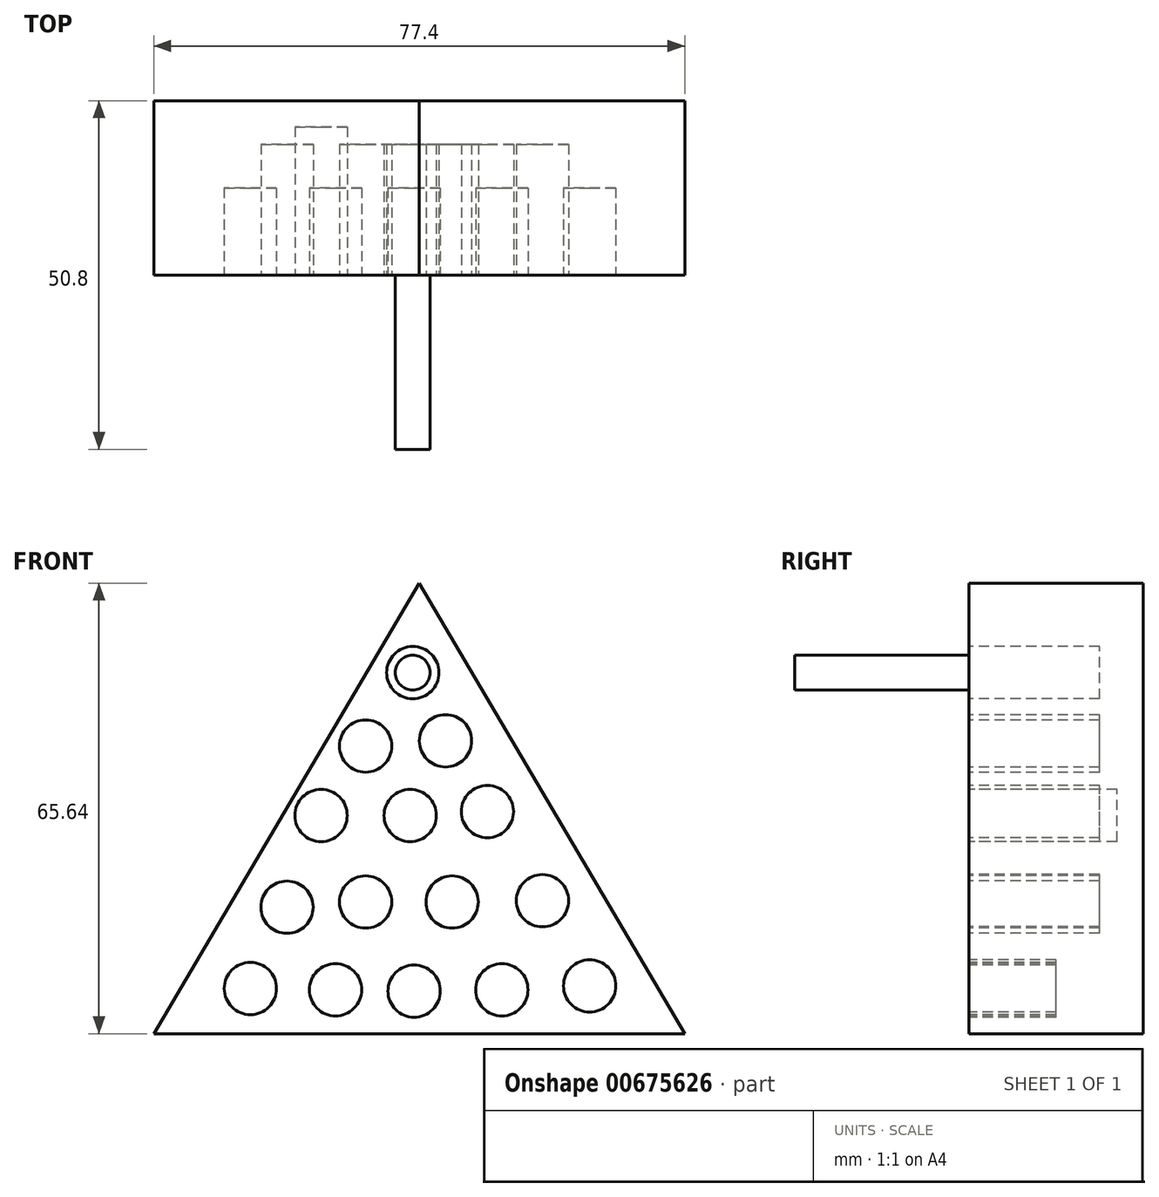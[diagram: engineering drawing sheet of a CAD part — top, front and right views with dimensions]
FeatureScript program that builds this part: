
annotation { "Feature Type Name" : "Feature", "Feature Type Description" : "" }
export const myFeature = defineFeature(function(context is Context, id is Id, definition is map)
    precondition{}
    {
        {
            var Q0;
            Q0=qCreatedBy(makeId("Front.planeOp"),FACE);
            var sketch = newSketch(context, id + "F0", { "sketchPlane" : qUnion([Q0])});
            skLineSegment(sketch, "E0", {"start": v(0, 0) * mm, "end": v(-38.7, 65.64) * mm});
            skLineSegment(sketch, "E1", {"start": v(-38.7, 65.64) * mm, "end": v(-77.4, 0) * mm});
            skLineSegment(sketch, "E2", {"start": v(-77.4, 0) * mm, "end": v(0, 0) * mm});
            skSolve(sketch);
        }
        {
            var Q0;
            Q0=makeQuery(id+"F0.imprint","IMPRINT",FACE,{"disambiguationData":[TD([[makeQuery(id+"F0.imprint","IMPRINT",EDGE,{"derivedFrom":sQuery(id+"F0.wireOp",EDGE,"E0")}),1.0]])]});
            extrude(context, id + "F1", {"entities" : qUnion([Q0]), "depth" : 25.4 * mm, "offsetDistance" : 25.4 * mm});
        }
        {
            var Q0;
            Q0=makeQuery(id+"F1.opExtrude","CAP_FACE",FACE,{"disambiguationData":[OSD([sQuery(id+"F0.wireOp",EDGE,"E0"),sQuery(id+"F0.wireOp",EDGE,"E1"),sQuery(id+"F0.wireOp",EDGE,"E2")])],"isStart":false});
            var sketch = newSketch(context, id + "F2", { "sketchPlane" : qUnion([Q0])});
            skCircle(sketch, "E3", {"center": v(-63.33, 6.59) * mm, "radius": 3.81 * mm});
            skCircle(sketch, "E4", {"center": v(-50.92, 6.4) * mm, "radius": 3.81 * mm});
            skCircle(sketch, "E5", {"center": v(-39.46, 6.2) * mm, "radius": 3.81 * mm});
            skCircle(sketch, "E6", {"center": v(-26.67, 6.4) * mm, "radius": 3.81 * mm});
            skCircle(sketch, "E7", {"center": v(-13.87, 6.97) * mm, "radius": 3.81 * mm});
            skSolve(sketch);
        }
        {
            var Q0;
            Q0 = qSketchRegion(id + "F2", true);
            extrude(context, id + "F3", {"entities" : qUnion([Q0]), "operationType" : NewBodyOperationType.REMOVE, "oppositeDirection" : true, "depth" : 12.7 * mm, "offsetDistance" : 25.4 * mm});
        }
        {
            var Q0;
            Q0=makeQuery(id+"F1.opExtrude","CAP_FACE",FACE,{"disambiguationData":[OSD([sQuery(id+"F0.wireOp",EDGE,"E0"),sQuery(id+"F0.wireOp",EDGE,"E1"),sQuery(id+"F0.wireOp",EDGE,"E2")])],"isStart":false});
            var sketch = newSketch(context, id + "F4", { "sketchPlane" : qUnion([Q0])});
            skCircle(sketch, "E8", {"center": v(-57.6, 19) * mm, "radius": 3.81 * mm});
            skSolve(sketch);
        }
        {
            var Q0;
            Q0=makeQuery(id+"F4.imprint","IMPRINT",FACE,{"disambiguationData":[TD([[makeQuery(id+"F4.imprint","IMPRINT",EDGE,{"derivedFrom":sQuery(id+"F4.wireOp",EDGE,"E8")}),-1.0]])]});
            var sketch = newSketch(context, id + "F5", { "sketchPlane" : qUnion([Q0])});
            skCircle(sketch, "E9", {"center": v(-46.52, 19.2) * mm, "radius": 3.81 * mm});
            skSolve(sketch);
        }
        {
            var Q0;
            Q0=makeQuery(id+"F4.imprint","IMPRINT",FACE,{"disambiguationData":[TD([[makeQuery(id+"F4.imprint","IMPRINT",EDGE,{"derivedFrom":sQuery(id+"F4.wireOp",EDGE,"E8")}),-1.0]])]});
            var sketch = newSketch(context, id + "F6", { "sketchPlane" : qUnion([Q0])});
            skCircle(sketch, "E10", {"center": v(-33.92, 19.2) * mm, "radius": 3.81 * mm});
            skSolve(sketch);
        }
        {
            var Q0;
            Q0=makeQuery(id+"F4.imprint","IMPRINT",FACE,{"disambiguationData":[TD([[makeQuery(id+"F4.imprint","IMPRINT",EDGE,{"derivedFrom":sQuery(id+"F4.wireOp",EDGE,"E8")}),-1.0]])]});
            var sketch = newSketch(context, id + "F7", { "sketchPlane" : qUnion([Q0])});
            skCircle(sketch, "E11", {"center": v(-20.75, 19.38) * mm, "radius": 3.81 * mm});
            skSolve(sketch);
        }
        {
            var Q0;
            Q0=makeQuery(id+"F4.imprint","IMPRINT",FACE,{"disambiguationData":[TD([[makeQuery(id+"F4.imprint","IMPRINT",EDGE,{"derivedFrom":sQuery(id+"F4.wireOp",EDGE,"E8")}),-1.0]])]});
            var sketch = newSketch(context, id + "F8", { "sketchPlane" : qUnion([Q0])});
            skCircle(sketch, "E12", {"center": v(-40.03, 31.8) * mm, "radius": 3.81 * mm});
            skSolve(sketch);
        }
        {
            var Q0;
            Q0=makeQuery(id+"F4.imprint","IMPRINT",FACE,{"disambiguationData":[TD([[makeQuery(id+"F4.imprint","IMPRINT",EDGE,{"derivedFrom":sQuery(id+"F4.wireOp",EDGE,"E8")}),-1.0]])]});
            var sketch = newSketch(context, id + "F9", { "sketchPlane" : qUnion([Q0])});
            skCircle(sketch, "E13", {"center": v(-53.02, 31.8) * mm, "radius": 3.81 * mm});
            skSolve(sketch);
        }
        {
            var Q0;
            Q0=makeQuery(id+"F7.imprint","IMPRINT",FACE,{"disambiguationData":[TD([[makeQuery(id+"F7.imprint","IMPRINT",EDGE,{"derivedFrom":sQuery(id+"F7.wireOp",EDGE,"E11")}),-1.0]])]});
            var sketch = newSketch(context, id + "F10", { "sketchPlane" : qUnion([Q0])});
            skCircle(sketch, "E14", {"center": v(-28.77, 32.37) * mm, "radius": 3.81 * mm});
            skSolve(sketch);
        }
        {
            var Q0;
            Q0=makeQuery(id+"F4.imprint","IMPRINT",FACE,{"disambiguationData":[TD([[makeQuery(id+"F4.imprint","IMPRINT",EDGE,{"derivedFrom":sQuery(id+"F4.wireOp",EDGE,"E8")}),-1.0]])]});
            var sketch = newSketch(context, id + "F11", { "sketchPlane" : qUnion([Q0])});
            skCircle(sketch, "E15", {"center": v(-46.52, 41.91) * mm, "radius": 3.81 * mm});
            skSolve(sketch);
        }
        {
            var Q0;
            Q0=makeQuery(id+"F4.imprint","IMPRINT",FACE,{"disambiguationData":[TD([[makeQuery(id+"F4.imprint","IMPRINT",EDGE,{"derivedFrom":sQuery(id+"F4.wireOp",EDGE,"E8")}),-1.0]])]});
            var sketch = newSketch(context, id + "F12", { "sketchPlane" : qUnion([Q0])});
            skCircle(sketch, "E16", {"center": v(-34.88, 42.68) * mm, "radius": 3.81 * mm});
            skSolve(sketch);
        }
        {
            var Q0;
            Q0=makeQuery(id+"F4.imprint","IMPRINT",FACE,{"disambiguationData":[TD([[makeQuery(id+"F4.imprint","IMPRINT",EDGE,{"derivedFrom":sQuery(id+"F4.wireOp",EDGE,"E8")}),-1.0]])]});
            var sketch = newSketch(context, id + "F13", { "sketchPlane" : qUnion([Q0])});
            skCircle(sketch, "E17", {"center": v(-39.65, 52.6) * mm, "radius": 3.81 * mm});
            skSolve(sketch);
        }
        {
            var Q0;
            Q0=makeQuery(id+"F4.imprint","IMPRINT",FACE,{"disambiguationData":[TD([[makeQuery(id+"F4.imprint","IMPRINT",EDGE,{"derivedFrom":sQuery(id+"F4.wireOp",EDGE,"E8")}),1.0]])]});
            extrude(context, id + "F14", {"entities" : qUnion([Q0]), "operationType" : NewBodyOperationType.REMOVE, "depth" : 25.4 * mm, "offsetDistance" : 25.4 * mm});
        }
        {
            var Q0;
            Q0=makeQuery(id+"F5.imprint","IMPRINT",FACE,{"disambiguationData":[TD([[makeQuery(id+"F5.imprint","IMPRINT",EDGE,{"derivedFrom":makeQuery(id+"F4.imprint","IMPRINT",EDGE,{"derivedFrom":sQuery(id+"F4.wireOp",EDGE,"E8")})}),1.0]])]});
            var sketch = newSketch(context, id + "F15", { "sketchPlane" : qUnion([Q0])});
            skCircle(sketch, "E18", {"center": v(-57.98, 18.43) * mm, "radius": 3.81 * mm});
            skSolve(sketch);
        }
        {
            var Q0;
            Q0 = qSketchRegion(id + "F5", true);
            extrude(context, id + "F16", {"entities" : qUnion([Q0]), "operationType" : NewBodyOperationType.REMOVE, "oppositeDirection" : true, "depth" : 19.05 * mm, "offsetDistance" : 25.4 * mm});
        }
        {
            var Q0;
            Q0 = qSketchRegion(id + "F6", true);
            extrude(context, id + "F17", {"entities" : qUnion([Q0]), "operationType" : NewBodyOperationType.REMOVE, "oppositeDirection" : true, "depth" : 19.05 * mm, "offsetDistance" : 25.4 * mm});
        }
        {
            var Q0;
            Q0 = qSketchRegion(id + "F8", true);
            extrude(context, id + "F18", {"entities" : qUnion([Q0]), "operationType" : NewBodyOperationType.REMOVE, "oppositeDirection" : true, "depth" : 19.05 * mm, "offsetDistance" : 25.4 * mm});
        }
        {
            var Q0;
            Q0 = qSketchRegion(id + "F7", true);
            extrude(context, id + "F19", {"entities" : qUnion([Q0]), "operationType" : NewBodyOperationType.REMOVE, "oppositeDirection" : true, "depth" : 19.05 * mm, "offsetDistance" : 25.4 * mm});
        }
        {
            var Q0;
            Q0 = qSketchRegion(id + "F12", true);
            extrude(context, id + "F20", {"entities" : qUnion([Q0]), "operationType" : NewBodyOperationType.REMOVE, "oppositeDirection" : true, "depth" : 19.05 * mm, "offsetDistance" : 25.4 * mm});
        }
        {
            var Q0;
            Q0 = qSketchRegion(id + "F13", true);
            extrude(context, id + "F21", {"entities" : qUnion([Q0]), "operationType" : NewBodyOperationType.REMOVE, "oppositeDirection" : true, "depth" : 19.05 * mm, "offsetDistance" : 25.4 * mm});
        }
        {
            var Q0;
            Q0 = qSketchRegion(id + "F11", true);
            extrude(context, id + "F22", {"entities" : qUnion([Q0]), "operationType" : NewBodyOperationType.REMOVE, "oppositeDirection" : true, "depth" : 19.05 * mm, "offsetDistance" : 25.4 * mm});
        }
        {
            var Q0;
            Q0 = qSketchRegion(id + "F9", true);
            extrude(context, id + "F23", {"entities" : qUnion([Q0]), "operationType" : NewBodyOperationType.REMOVE, "oppositeDirection" : true, "depth" : 21.59 * mm, "offsetDistance" : 25.4 * mm});
        }
        {
            var Q0;
            Q0 = qSketchRegion(id + "F15", true);
            extrude(context, id + "F24", {"entities" : qUnion([Q0]), "operationType" : NewBodyOperationType.REMOVE, "oppositeDirection" : true, "depth" : 19.05 * mm, "offsetDistance" : 25.4 * mm});
        }
        {
            var Q0;
            Q0 = qSketchRegion(id + "F10", true);
            extrude(context, id + "F25", {"entities" : qUnion([Q0]), "operationType" : NewBodyOperationType.REMOVE, "oppositeDirection" : true, "depth" : 19.05 * mm, "offsetDistance" : 25.4 * mm});
        }
        {
            var Q0;
            Q0=makeQuery(id+"F1.opExtrude","CAP_FACE",FACE,{"disambiguationData":[OSD([sQuery(id+"F0.wireOp",EDGE,"E0"),sQuery(id+"F0.wireOp",EDGE,"E1"),sQuery(id+"F0.wireOp",EDGE,"E2")])],"isStart":false});
            var sketch = newSketch(context, id + "F26", { "sketchPlane" : qUnion([Q0])});
            skCircle(sketch, "E19", {"center": v(-39.65, 52.6) * mm, "radius": 2.54 * mm});
            skSolve(sketch);
        }
        {
            var Q0;
            Q0 = qSketchRegion(id + "F26", true);
            extrude(context, id + "F27", {"entities" : qUnion([Q0]), "depth" : 25.4 * mm, "offsetDistance" : 25.4 * mm});
        }
    });
